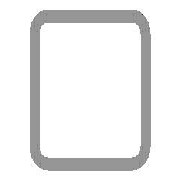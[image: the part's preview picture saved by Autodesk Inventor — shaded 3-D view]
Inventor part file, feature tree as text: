
AUTODESK INVENTOR PART (.ipt)
format: ipt  version: 2025.1 (Build 291241020, 241B)  size: 131,584 bytes
history: native  units: mm (DEFAULTED — no unit token found)
features: other x4, sketch x1, plane x1
ambient origin geometry x8: Origin, YZ Plane, XZ Plane, XY Plane, X Axis, Y Axis, Z Axis, Center Point
bodies: Solid1 (feature_tree), Body (feature_tree)
feature tree (6):
  parser-record x1  (decoder bookkeeping rows leaked as tree rows — omitted from the tree; the rows remain in map.json)
  other  "Driven Length"
  other  "Start Plane"
  other  "End Plane"
  sketch  "Sketch3"  dims[d3=848.528137mm d4=0.0mm d7=4.0mm d9=40.0mm d11=40.0mm d12=2.0mm d13=-0.0mm d14=848.528137mm d15=20.0mm d16=20.0mm d17=90.0deg d18=848.528137mm]
  plane  "Work Plane3"
